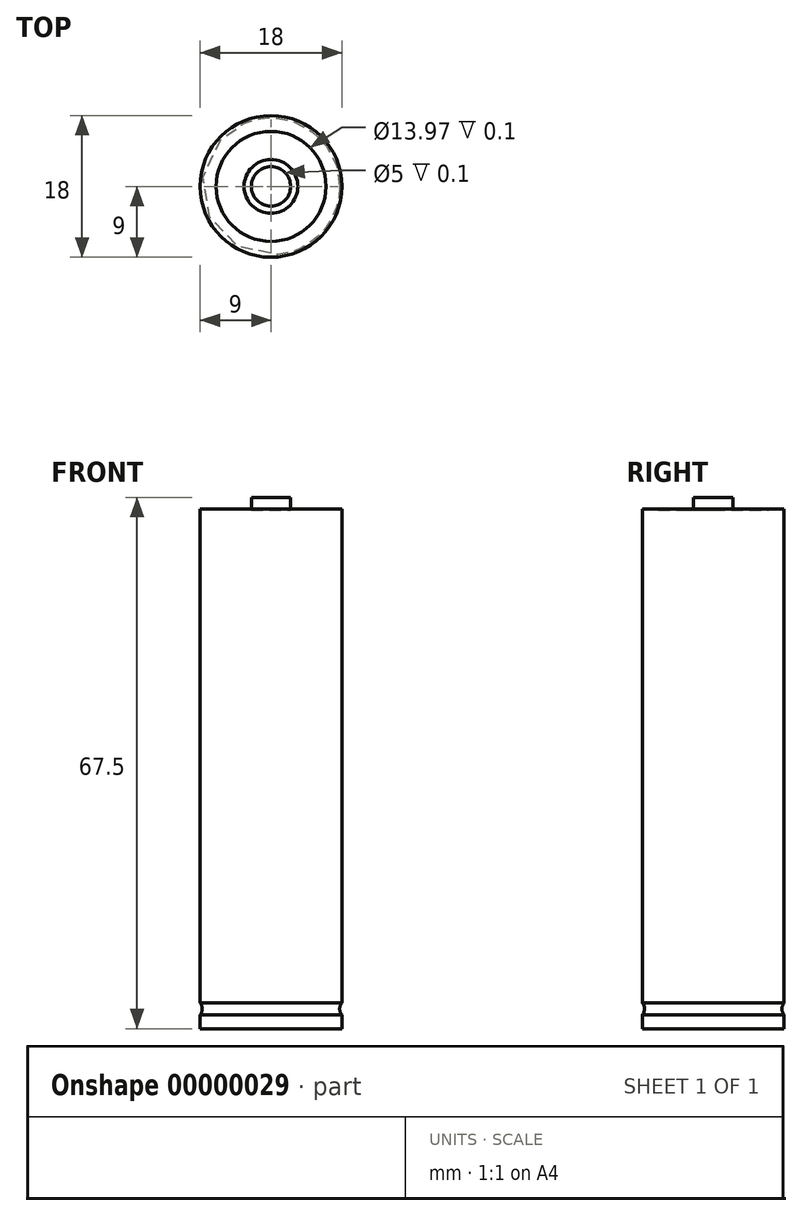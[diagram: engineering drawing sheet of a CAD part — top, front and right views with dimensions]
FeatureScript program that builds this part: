
annotation { "Feature Type Name" : "Feature", "Feature Type Description" : "" }
export const myFeature = defineFeature(function(context is Context, id is Id, definition is map)
    precondition{}
    {
        {
            var Q0;
            Q0=qCreatedBy(makeId("Front.planeOp"),FACE);
            var sketch = newSketch(context, id + "F0", { "sketchPlane" : qUnion([Q0])});
            skLineSegment(sketch, "E0", {"start": v(0, 0) * mm, "end": v(9, 0) * mm});
            skLineSegment(sketch, "E1", {"start": v(9, 0) * mm, "end": v(9, 66) * mm});
            skLineSegment(sketch, "E2", {"start": v(9, 66) * mm, "end": v(2.5, 66) * mm});
            skLineSegment(sketch, "E3", {"start": v(2.5, 66) * mm, "end": v(2.5, 67.5) * mm});
            skLineSegment(sketch, "E4", {"start": v(2.5, 67.5) * mm, "end": v(0, 67.5) * mm});
            skLineSegment(sketch, "E5", {"start": v(0, -1.12) * mm, "end": v(0, 67.5) * mm});
            skSolve(sketch);
        }
        {
            var Q0;
            {var subQ2=sQuery(id+"F0.wireOp",EDGE,"E0");Q0=makeQuery(id+"F0.imprint","IMPRINT",FACE,{"disambiguationData":[TD([[makeQuery(id+"F0.imprint","IMPRINT",EDGE,{"derivedFrom":subQ2}),1.0]])]});}
            var Q1;
            Q1=sQuery(id+"F0.wireOp",EDGE,"E5");
            revolve(context, id + "F1", {"entities" : qUnion([Q0]), "axis" : qUnion([Q1]), "revolveType" : RevolveType.FULL});
        }
        {
            var Q0;
            Q0=makeQuery(id+"F1.opRevolve","SWEPT_FACE",FACE,{"disambiguationData":[OSD([sQuery(id+"F0.wireOp",EDGE,"E2")])]});
            var sketch = newSketch(context, id + "F2", { "sketchPlane" : qUnion([Q0])});
            skCircle(sketch, "E6", {"center": v(0, 0) * mm, "radius": 6.98 * mm});
            skCircle(sketch, "E7", {"center": v(0, 0) * mm, "radius": 3.41 * mm});
            skSolve(sketch);
        }
        {
            var Q0;
            Q0=makeQuery(id+"F2.imprint","IMPRINT",FACE,{"disambiguationData":[TD([[makeQuery(id+"F2.imprint","IMPRINT",EDGE,{"derivedFrom":makeQuery(id+"F1.opRevolve","SWEPT_EDGE",EDGE,{"disambiguationData":[OSD([sQuery(id+"F0.wireOp",EDGE,"E2"),sQuery(id+"F0.wireOp",EDGE,"E3")])]})}),-1.0]])]});
            var Q1;
            Q1=makeQuery(id+"F2.imprint","IMPRINT",FACE,{"disambiguationData":[TD([[makeQuery(id+"F2.imprint","IMPRINT",EDGE,{"derivedFrom":sQuery(id+"F2.wireOp",EDGE,"E6")}),1.0]])]});
            extrude(context, id + "F3", {"entities" : qUnion([Q0, Q1]), "operationType" : NewBodyOperationType.REMOVE, "oppositeDirection" : true, "depth" : 0.1 * mm});
        }
        {
            var Q0;
            Q0=qCreatedBy(makeId("Right.planeOp"),FACE);
            var sketch = newSketch(context, id + "F4", { "sketchPlane" : qUnion([Q0])});
            skCircle(sketch, "E8", {"center": v(9.9, 2.52) * mm, "radius": 1.17 * mm});
            skLineSegment(sketch, "E9", {"start": v(0, 0) * mm, "end": v(0, 3.87) * mm, "construction": true});
            skSolve(sketch);
        }
        {
            var Q0;
            Q0=makeQuery(id+"F4.imprint","IMPRINT",FACE,{"disambiguationData":[TD([[makeQuery(id+"F4.imprint","IMPRINT",EDGE,{"derivedFrom":sQuery(id+"F4.wireOp",EDGE,"E8")}),1.0]])]});
            var Q1;
            Q1=sQuery(id+"F4.wireOp",EDGE,"E9");
            revolve(context, id + "F5", {"operationType" : NewBodyOperationType.REMOVE, "entities" : qUnion([Q0]), "axis" : qUnion([Q1]), "revolveType" : RevolveType.FULL, "oppositeDirection" : true});
        }
    });
